# Revit family: Vitra_S20_UndercounterWashBasin_5475B003-0618
name_source: partatom
category: Plumbing Fixtures
revit_build: Autodesk Revit 2017 (Build: 20160225_1515(x64)
units: mm (PartAtom-declared; Revit-internal decimal feet)

## family parameters
Cut with Voids When Loaded = No
Host = Face
OmniClass Number = 23.45.05.14.14
OmniClass Title = Sinks/Lavatories
Part Type = Normal
Room Calculation Point = No
Round Connector Dimension = Use Diameter
Shared = Yes

## types (1)
- WashBasin(Undercounter)-Vitra_S20 Series_5475B003-0618
    Article No. (default) = 5475B003-0618
    BIMobject category = Sanitary - Basins
    CW Connection = No
    Color = White
    Cost = 0 $
    Default Elevation = 850 mm  [stored 2.78871 ft]
    Description = VitrA S20
    Design country = Turkey
    HW Connection = No
    IFC Classification = Sanitary Terminal
    Main Material = Ceramic
    Manufacturer = Vitra
    Manufacturer name = Vitra
    Masterformat 2014 Code = 22 41 16
    Masterformat 2014 Description = Residential Lavatories and Sinks
    Model = 5475B003-0618
    MountingType = Undercounter
    NBS Referans Code = 35-65-70-94
    NBS Referans Description = Wash Basin Systems
    Nominal Depth = 370 mm  [stored 1.21391 ft]
    NominalHeight = 165 mm
    NominalWidth = 550 mm
    OmniClass Code = 23.45.05.14.14
    OmniClass Description = Sinks/Lavatories
    Product SKU = 5475B003-0618
    Product certification = https://vitraglobal.com
    Product data url = https://www.vitra.com.tr
    Product family = Undercounter Washbasins
    Product group = S20
    Secondary Material = Vitra-Ceramic-White
    Technical description = https://www.vitra.com.tr
    UNSPSC Code = 301815
    URL = https://vitraglobal.com
    Uniclass 1.4 Code = L7212
    Uniclass 1.4 Description = Washbasins
    Uniclass 2.0 Code = SS-35-65-70-94
    Uniclass 2.0 Description = Sanitary Dispensing And Disposal Units
    Uniclass 2015 Code = Pr_40_20_96_81
    Uniclass 2015 Name = Wash basins, Sinks and troughs
    Uniformat II Code = D2010
    Uniformat II Description = Plumbing Fixtures
    Vent Connection = No
    Warranty Period (Year) = 10 Years
    Waste Connection = Yes
    Weight Net (kg) = 10,836
    Youtube = https://www.youtube.com

note: [stored X ft] marks values corroborated as IEEE doubles in the binary element streams (Revit-internal decimal feet)

## geometry (parser evidence)
native form markers: Sweep x3
no freeform markers — native parametric forms only
